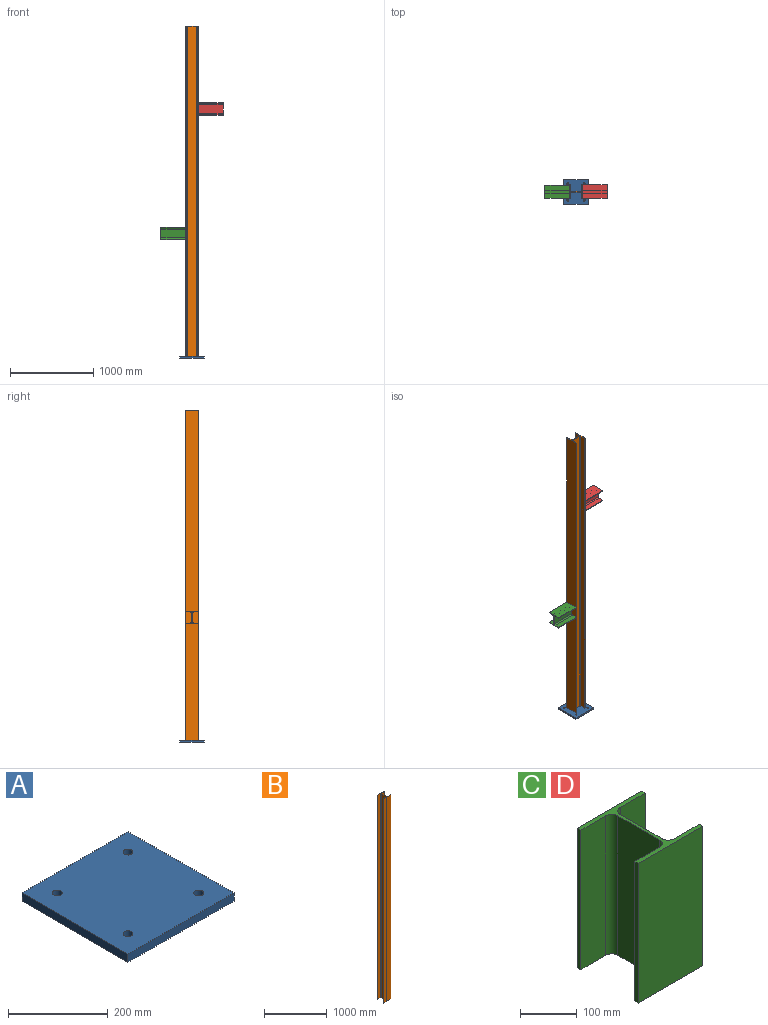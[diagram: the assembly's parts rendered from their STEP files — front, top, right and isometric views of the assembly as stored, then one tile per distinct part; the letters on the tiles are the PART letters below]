
ASSEMBLY  parts=4 mates=3
PART A: 10 faces, bbox 300x300x20 mm
  f0: plane 300x20mm, normal (1,0,0), area 6000mm2, adj f1,f6,f8,f9
  f1: plane 300x20mm, normal (0,1,0), area 6000mm2, adj f0,f2,f8,f9
  f2: plane 300x20mm, normal (-1,0,0), area 6000mm2, adj f1,f6,f8,f9
  f3: cylinder r=10mm len=20mm, axis (0,0,-1), area 1256.6mm2, adj f8,f9
  f4: cylinder r=10mm len=20mm, axis (0,0,-1), area 1256.6mm2, adj f8,f9
  f5: cylinder r=10mm len=20mm, axis (0,0,-1), area 1256.6mm2, adj f8,f9
  f6: plane 300x20mm, normal (0,-1,0), area 6000mm2, adj f0,f2,f8,f9
  f7: cylinder r=10mm len=20mm, axis (0,0,-1), area 1256.6mm2, adj f8,f9
  f8: plane 300x300mm, normal (0,0,1), area 88743.4mm2, adj f0,f1,f2,f3,f4,f5,f6,f7
  f9: plane 300x300mm, normal (0,0,-1), area 88743.4mm2, adj f0,f1,f2,f3,f4,f5,f6,f7
PART B: 18 faces, bbox 160x152x3980 mm
  f0: plane 3980x9mm, normal (-1,0,0), area 35820mm2, adj f1,f15,f16,f17
  f1: plane 3980x62mm, normal (0,1,0), area 246760mm2, adj f0,f2,f16,f17
  f2: cylinder r=15mm len=3980mm, axis (0,0,1), area 93776.5mm2, adj f1,f3,f16,f17
  f3: plane 3980x104mm, normal (-1,0,0), area 413920mm2, adj f2,f4,f16,f17
  f4: cylinder r=15mm len=3980mm, axis (0,0,1), area 93776.5mm2, adj f3,f5,f16,f17
  f5: plane 3980x62mm, normal (0,-1,0), area 246760mm2, adj f4,f6,f16,f17
  f6: plane 3980x9mm, normal (-1,0,0), area 35820mm2, adj f5,f7,f16,f17
  f7: plane 3980x160mm, normal (0,1,0), area 636800mm2, adj f6,f8,f16,f17
  f8: plane 3980x9mm, normal (1,0,0), area 35820mm2, adj f7,f9,f16,f17
  f9: plane 3980x62mm, normal (0,-1,0), area 246760mm2, adj f8,f10,f16,f17
  f10: cylinder r=15mm len=3980mm, axis (0,0,1), area 93776.5mm2, adj f9,f11,f16,f17
  f11: plane 3980x104mm, normal (1,0,0), area 413920mm2, adj f10,f12,f16,f17
  f12: cylinder r=15mm len=3980mm, axis (0,0,1), area 93776.5mm2, adj f11,f13,f16,f17
  f13: plane 3980x62mm, normal (0,1,0), area 246760mm2, adj f12,f14,f16,f17
  f14: plane 3980x9mm, normal (1,0,0), area 35820mm2, adj f13,f15,f16,f17
  f15: plane 3980x160mm, normal (0,-1,0), area 636800mm2, adj f0,f14,f16,f17
  f16: plane 160x152mm, normal (0,0,1), area 3877.1mm2, adj f0,f1,f2,f3,f4,f5,f6,f7
  f17: plane 160x152mm, normal (0,0,-1), area 3877.1mm2, adj f0,f1,f2,f3,f4,f5,f6,f7
PART C: 18 faces, bbox 160x152x300 mm
  f0: plane 300x9mm, normal (-1,0,0), area 2700mm2, adj f1,f15,f16,f17
  f1: plane 300x62mm, normal (0,1,0), area 18600mm2, adj f0,f2,f16,f17
  f2: cylinder r=15mm len=300mm, axis (0,0,1), area 7068.6mm2, adj f1,f3,f16,f17
  f3: plane 300x104mm, normal (-1,0,0), area 31200mm2, adj f2,f4,f16,f17
  f4: cylinder r=15mm len=300mm, axis (0,0,1), area 7068.6mm2, adj f3,f5,f16,f17
  f5: plane 300x62mm, normal (0,-1,0), area 18600mm2, adj f4,f6,f16,f17
  f6: plane 300x9mm, normal (-1,0,0), area 2700mm2, adj f5,f7,f16,f17
  f7: plane 300x160mm, normal (0,1,0), area 48000mm2, adj f6,f8,f16,f17
  f8: plane 300x9mm, normal (1,0,0), area 2700mm2, adj f7,f9,f16,f17
  f9: plane 300x62mm, normal (0,-1,0), area 18600mm2, adj f8,f10,f16,f17
  f10: cylinder r=15mm len=300mm, axis (0,0,1), area 7068.6mm2, adj f9,f11,f16,f17
  f11: plane 300x104mm, normal (1,0,0), area 31200mm2, adj f10,f12,f16,f17
  f12: cylinder r=15mm len=300mm, axis (0,0,1), area 7068.6mm2, adj f11,f13,f16,f17
  f13: plane 300x62mm, normal (0,1,0), area 18600mm2, adj f12,f14,f16,f17
  f14: plane 300x9mm, normal (1,0,0), area 2700mm2, adj f13,f15,f16,f17
  f15: plane 300x160mm, normal (0,-1,0), area 48000mm2, adj f0,f14,f16,f17
  f16: plane 160x152mm, normal (0,0,1), area 3877.1mm2, adj f0,f1,f2,f3,f4,f5,f6,f7
  f17: plane 160x152mm, normal (0,0,-1), area 3877.1mm2, adj f0,f1,f2,f3,f4,f5,f6,f7
PART D: same geometry as C
PLACE A at identity
PLACE B rot(axis=(0,0,1),90deg) t=(0,0,2010)mm
PLACE C rot(axis=(0.58,-0.58,-0.58),120deg) t=(-226,0,1500)mm
PLACE D rot(axis=(0.58,-0.58,-0.58),120deg) t=(226,0,3000)mm
MATE fastened B.f17 <-> A.f8  axis (0,0,-1) through (0,0,20)mm
MATE fastened D.f16 <-> B.f15  axis (-1,0,0) through (76,0,3000)mm
MATE fastened C.f17 <-> B.f7  axis (1,0,0) through (-76,0,1500)mm
